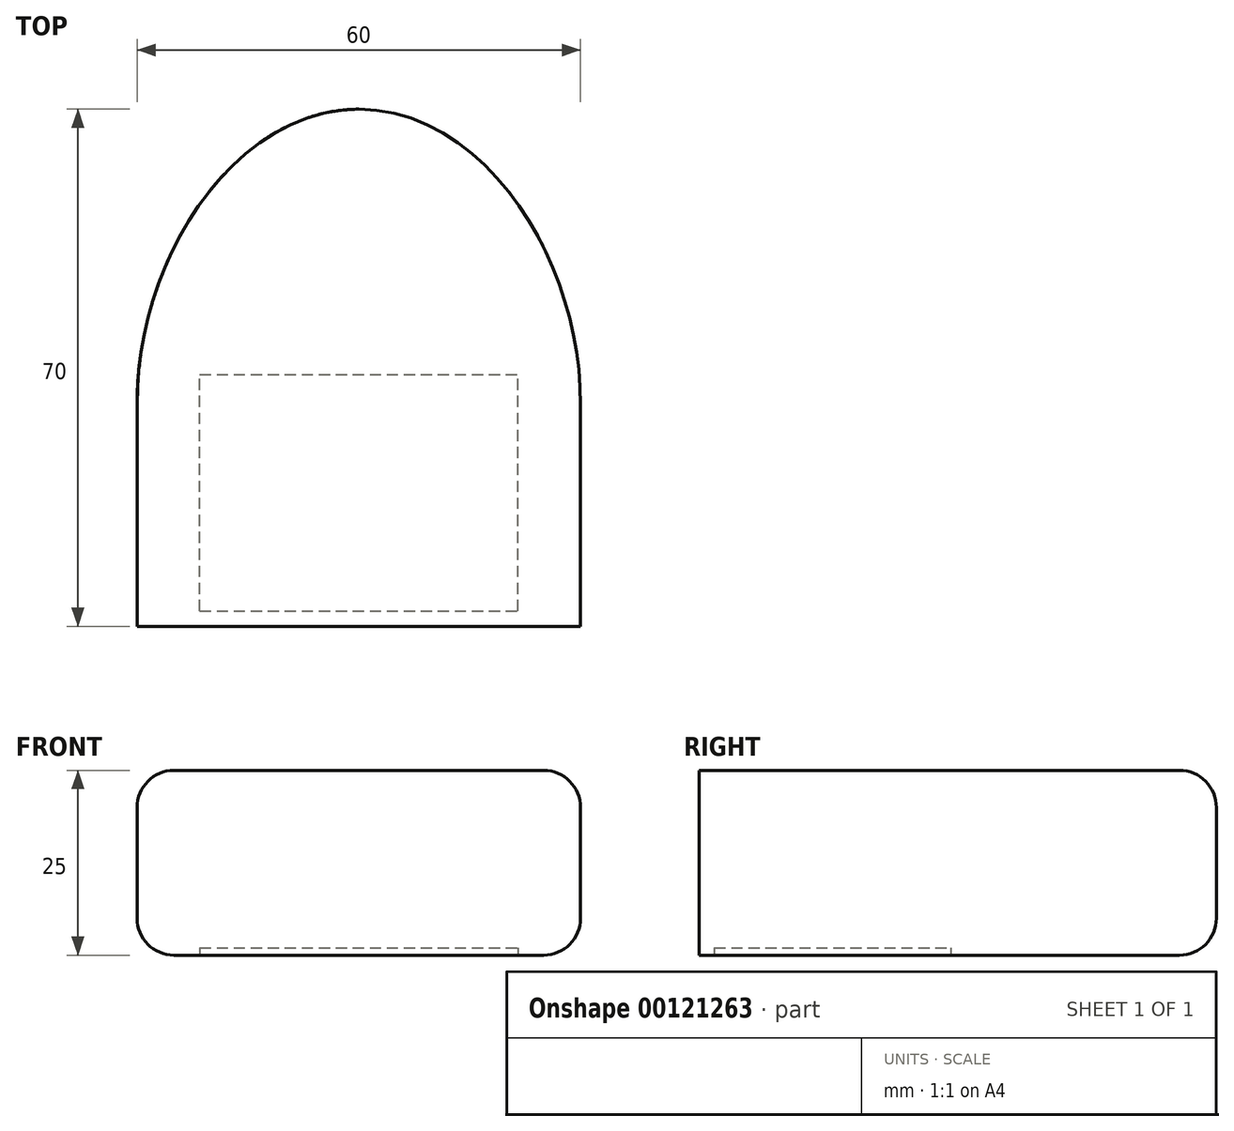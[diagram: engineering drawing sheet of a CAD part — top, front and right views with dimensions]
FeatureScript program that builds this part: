
annotation { "Feature Type Name" : "Feature", "Feature Type Description" : "" }
export const myFeature = defineFeature(function(context is Context, id is Id, definition is map)
    precondition{}
    {
        {
            var Q0;
            Q0=qCreatedBy(makeId("Top.planeOp"),FACE);
            var sketch = newSketch(context, id + "F0", { "sketchPlane" : qUnion([Q0])});
            skLineSegment(sketch, "E0.top", {"start": v(-30, -38.1) * mm, "end": v(30, -38.1) * mm});
            skPoint(sketch, "E0.middle", {"position": v(0, 0) * mm});
            skPoint(sketch, "E1", {"position": v(0, -8.1) * mm});
            skCircle(sketch, "E2", {"center": v(0, -8.1) * mm, "radius": 30 * mm});
            skPoint(sketch, "E3.visualSharp", {"position": v(-30, -38.1) * mm});
            skPoint(sketch, "E4.visualSharp", {"position": v(30, -38.1) * mm});
            skPoint(sketch, "E5", {"position": v(-30, -8.1) * mm});
            skPoint(sketch, "E6", {"position": v(30, -8.1) * mm});
            skFitSpline(sketch, "E7", {"points": [v(0, 31.9) * mm, v(-30, -8.1) * mm], "startDerivative": vector(-49.89, 0) * mm, "endDerivative": vector(0, -60.15) * mm});
            skFitSpline(sketch, "E8.MirrorCS", {"points": [v(0, 31.9) * mm, v(30, -8.1) * mm], "startDerivative": vector(49.89, 0) * mm, "endDerivative": vector(0, -60.15) * mm});
            skLineSegment(sketch, "E9", {"start": v(-30, -8.1) * mm, "end": v(-30, -38.1) * mm});
            skLineSegment(sketch, "E10", {"start": v(30, -8.1) * mm, "end": v(30, -38.1) * mm});
            skSolve(sketch);
        }
        {
            var Q0;
            Q0 = qSketchRegion(id + "F0", true);
            extrude(context, id + "F1", {"entities" : qUnion([Q0]), "endBound" : BoundingType.SYMMETRIC, "depth" : 25 * mm});
        }
        {
            var Q0;
            Q0=makeQuery(id+"F1.opExtrude","CAP_EDGE",EDGE,{"disambiguationData":[OSD([sQuery(id+"F0.wireOp",EDGE,"E10")])],"isStart":true});
            var Q1;
            Q1=makeQuery(id+"F1.opExtrude","CAP_EDGE",EDGE,{"disambiguationData":[OSD([sQuery(id+"F0.wireOp",EDGE,"E10")])],"isStart":false});
            var Q2;
            Q2=makeQuery(id+"F1.opExtrude","CAP_EDGE",EDGE,{"disambiguationData":[OSD([sQuery(id+"F0.wireOp",EDGE,"E9")])],"isStart":false});
            var Q3;
            Q3=makeQuery(id+"F1.opExtrude","CAP_EDGE",EDGE,{"disambiguationData":[OSD([sQuery(id+"F0.wireOp",EDGE,"E9")])],"isStart":true});
            fillet(context, id + "F2", {"entities" : qUnion([Q0, Q1, Q2, Q3]), "radius" : 5 * mm, "tangentPropagation" : true, "allowEdgeOverflow" : false});
        }
        {
            var Q0;
            Q0=makeQuery(id+"F1.opExtrude","CAP_FACE",FACE,{"disambiguationData":[OSD([sQuery(id+"F0.wireOp",EDGE,"E0.top"),sQuery(id+"F0.wireOp",EDGE,"E7"),sQuery(id+"F0.wireOp",EDGE,"E8.MirrorCS"),sQuery(id+"F0.wireOp",EDGE,"E9"),sQuery(id+"F0.wireOp",EDGE,"E10")])],"isStart":true});
            var sketch = newSketch(context, id + "F3", { "sketchPlane" : qUnion([Q0])});
            skLineSegment(sketch, "E11.bottom", {"start": v(-21.5, 36) * mm, "end": v(21.5, 36) * mm});
            skLineSegment(sketch, "E11.top", {"start": v(-21.5, 4) * mm, "end": v(21.5, 4) * mm});
            skLineSegment(sketch, "E11.left", {"start": v(-21.5, 36) * mm, "end": v(-21.5, 4) * mm});
            skLineSegment(sketch, "E11.right", {"start": v(21.5, 36) * mm, "end": v(21.5, 4) * mm});
            skPoint(sketch, "E11.middle", {"position": v(0, 20) * mm});
            skSolve(sketch);
        }
        {
            var Q0;
            Q0 = qSketchRegion(id + "F3", true);
            var Q1;
            Q1=makeQuery(id+"F3.imprint","IMPRINT",FACE,{"disambiguationData":[TD([[makeQuery(id+"F3.imprint","IMPRINT",EDGE,{"derivedFrom":sQuery(id+"F3.wireOp",EDGE,"E11.bottom")}),-1.0]])]});
            extrude(context, id + "F4", {"entities" : qUnion([Q0, Q1]), "operationType" : NewBodyOperationType.REMOVE, "oppositeDirection" : true, "depth" : 1 * mm});
        }
    });
